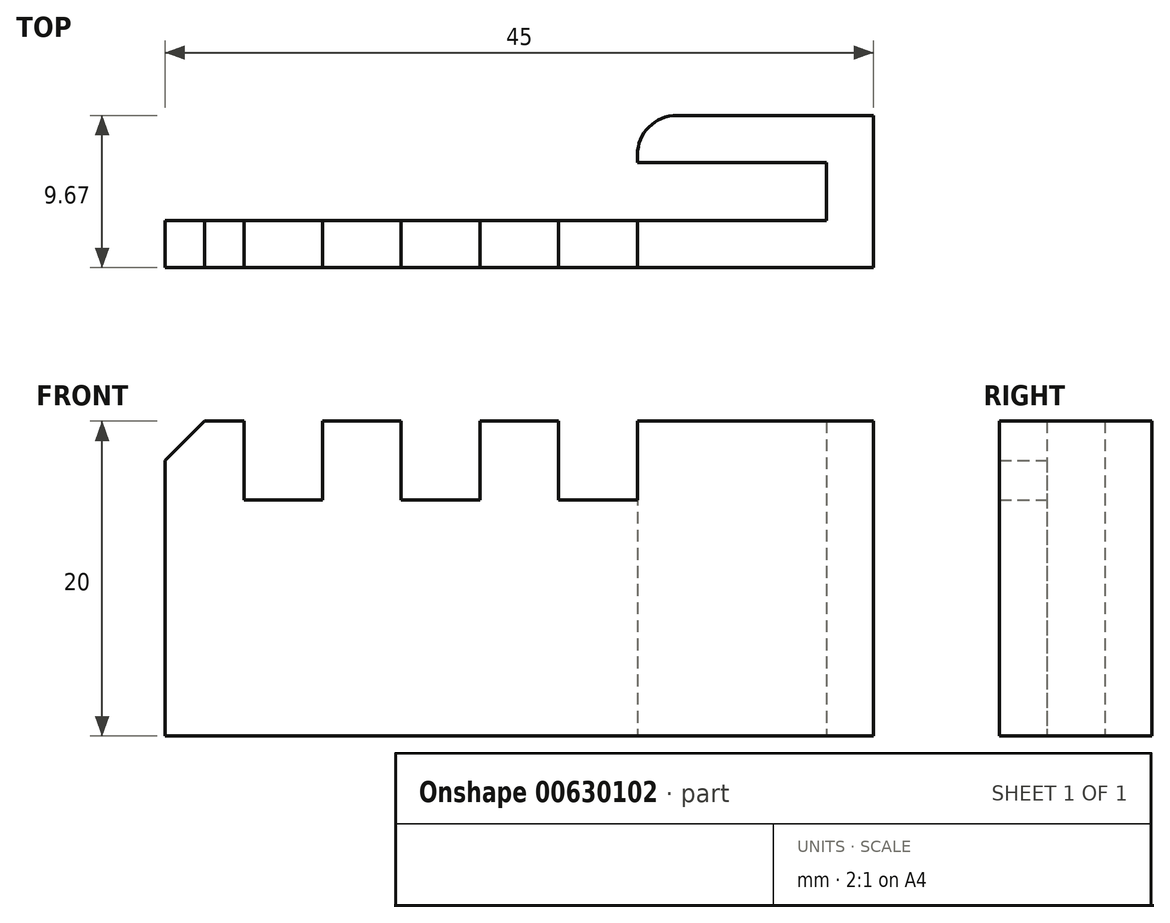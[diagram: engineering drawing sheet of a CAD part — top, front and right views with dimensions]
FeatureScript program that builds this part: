
annotation { "Feature Type Name" : "Feature", "Feature Type Description" : "" }
export const myFeature = defineFeature(function(context is Context, id is Id, definition is map)
    precondition{}
    {
        {
            var Q0;
            Q0=qCreatedBy(makeId("Top.planeOp"),FACE);
            var sketch = newSketch(context, id + "F0", { "sketchPlane" : qUnion([Q0])});
            skLineSegment(sketch, "E0", {"start": v(0, -4.53) * mm, "end": v(-15, -4.53) * mm});
            skLineSegment(sketch, "E1", {"start": v(-15, -4.53) * mm, "end": v(-15, -7.53) * mm});
            skLineSegment(sketch, "E2", {"start": v(-15, -7.53) * mm, "end": v(-3, -7.53) * mm});
            skLineSegment(sketch, "E3", {"start": v(-3, -7.53) * mm, "end": v(-3, -11.2) * mm});
            skLineSegment(sketch, "E4", {"start": v(-3, -11.2) * mm, "end": v(-45, -11.2) * mm});
            skLineSegment(sketch, "E5", {"start": v(0, -14.2) * mm, "end": v(-45, -14.2) * mm});
            skLineSegment(sketch, "E6", {"start": v(-45, -14.2) * mm, "end": v(-45, -11.2) * mm});
            skLineSegment(sketch, "E7", {"start": v(0, -4.53) * mm, "end": v(0, -14.2) * mm});
            skSolve(sketch);
        }
        {
            var Q0;
            Q0=makeQuery(id+"F0.imprint","IMPRINT",FACE,{"disambiguationData":[TD([[makeQuery(id+"F0.imprint","IMPRINT",EDGE,{"derivedFrom":sQuery(id+"F0.wireOp",EDGE,"E0")}),1.0]])]});
            extrude(context, id + "F1", {"entities" : qUnion([Q0]), "depth" : 20 * mm, "offsetDistance" : 25 * mm});
        }
        {
            var Q0;
            Q0=qCreatedBy(makeId("Front.planeOp"),FACE);
            var sketch = newSketch(context, id + "F2", { "sketchPlane" : qUnion([Q0])});
            skLineSegment(sketch, "E8.0.0", {"start": v(-45, 0) * mm, "end": v(0, 0) * mm});
            skLineSegment(sketch, "E8.0.1", {"start": v(0, 0) * mm, "end": v(0, 20) * mm});
            skLineSegment(sketch, "E8.0.2", {"start": v(0, 20) * mm, "end": v(-45, 20) * mm});
            skLineSegment(sketch, "E8.0.3", {"start": v(-45, 20) * mm, "end": v(-45, 0) * mm});
            skLineSegment(sketch, "E9", {"start": v(-15, 17.45) * mm, "end": v(-15, 20) * mm});
            skLineSegment(sketch, "E10", {"start": v(-15, 20) * mm, "end": v(-15, 15) * mm});
            skLineSegment(sketch, "E11", {"start": v(-15, 15) * mm, "end": v(-20, 15) * mm});
            skLineSegment(sketch, "E12", {"start": v(-20, 15) * mm, "end": v(-20, 20) * mm});
            skLineSegment(sketch, "E13", {"start": v(-20, 20) * mm, "end": v(-25, 20) * mm});
            skLineSegment(sketch, "E14", {"start": v(-25, 20) * mm, "end": v(-25, 15) * mm});
            skLineSegment(sketch, "E15", {"start": v(-25, 15) * mm, "end": v(-30, 15) * mm});
            skLineSegment(sketch, "E16", {"start": v(-30, 15) * mm, "end": v(-30, 20) * mm});
            skLineSegment(sketch, "E17", {"start": v(-30, 20) * mm, "end": v(-35, 20) * mm});
            skLineSegment(sketch, "E18", {"start": v(-35, 20) * mm, "end": v(-35, 15) * mm});
            skLineSegment(sketch, "E19", {"start": v(-15, 20) * mm, "end": v(0, 20) * mm});
            skLineSegment(sketch, "E20", {"start": v(-35, 15) * mm, "end": v(-40, 15) * mm});
            skLineSegment(sketch, "E21", {"start": v(-40, 15) * mm, "end": v(-40, 20) * mm});
            skSolve(sketch);
        }
        {
            var Q0;
            {var subQ0=sQuery(id+"F2.wireOp",EDGE,"p39oFGg6-OyMy-OwiJ-dlir-hBi66J1yGtTy");Q0=makeQuery(id+"F2.imprint","IMPRINT",FACE,{"disambiguationData":[TD([[makeQuery(id+"F2.imprint","IMPRINT",EDGE,{"derivedFrom":subQ0}),1.0]])]});}
            var Q1;
            {var subQ0=sQuery(id+"F2.wireOp",EDGE,"QODlYd0c-C4PW-zkeU-aZbA-vr5giQBnZzte");Q1=makeQuery(id+"F2.imprint","IMPRINT",FACE,{"disambiguationData":[TD([[makeQuery(id+"F2.imprint","IMPRINT",EDGE,{"derivedFrom":subQ0}),1.0]])]});}
            var Q2;
            {var subQ0=sQuery(id+"F2.wireOp",EDGE,"4xKgk40Y-SCAd-XMLl-Py7b-CMe8KArE31fU");Q2=makeQuery(id+"F2.imprint","IMPRINT",FACE,{"disambiguationData":[TD([[makeQuery(id+"F2.imprint","IMPRINT",EDGE,{"derivedFrom":subQ0}),1.0]])]});}
            var Q3;
            {var subQ0=sQuery(id+"F2.wireOp",EDGE,"CYAmrffy-ebrT-692H-EbRy-YjbJ9vrfb0BI");Q3=makeQuery(id+"F2.imprint","IMPRINT",FACE,{"disambiguationData":[TD([[makeQuery(id+"F2.imprint","IMPRINT",EDGE,{"derivedFrom":subQ0}),1.0]])]});}
            var Q4;
            {var subQ0=sQuery(id+"F2.wireOp",EDGE,"4ANwyr2W-lThm-HwLl-JWs1-NF0Ujadkufbg");Q4=makeQuery(id+"F2.imprint","IMPRINT",FACE,{"disambiguationData":[TD([[makeQuery(id+"F2.imprint","IMPRINT",EDGE,{"derivedFrom":subQ0}),1.0]])]});}
            var Q5;
            {var subQ0=sQuery(id+"F2.wireOp",EDGE,"E11");Q5=makeQuery(id+"F2.imprint","IMPRINT",FACE,{"disambiguationData":[TD([[makeQuery(id+"F2.imprint","IMPRINT",EDGE,{"derivedFrom":subQ0}),-1.0]])]});}
            var Q6;
            {var subQ0=sQuery(id+"F2.wireOp",EDGE,"E14");Q6=makeQuery(id+"F2.imprint","IMPRINT",FACE,{"disambiguationData":[TD([[makeQuery(id+"F2.imprint","IMPRINT",EDGE,{"derivedFrom":subQ0}),-1.0]])]});}
            var Q7;
            {var subQ0=sQuery(id+"F2.wireOp",EDGE,"E18");Q7=makeQuery(id+"F2.imprint","IMPRINT",FACE,{"disambiguationData":[TD([[makeQuery(id+"F2.imprint","IMPRINT",EDGE,{"derivedFrom":subQ0}),-1.0]])]});}
            extrude(context, id + "F3", {"entities" : qUnion([Q0, Q1, Q2, Q3, Q4, Q5, Q6, Q7]), "operationType" : NewBodyOperationType.REMOVE, "endBound" : BoundingType.THROUGH_ALL, "depth" : 25 * mm, "offsetDistance" : 25 * mm});
        }
        {
            var Q0;
            Q0=makeQuery(id+"F1.opExtrude","CAP_EDGE",EDGE,{"disambiguationData":[OSD([sQuery(id+"F0.wireOp",EDGE,"E6")])],"isStart":false});
            chamfer(context, id + "F4", {"entities" : qUnion([Q0]), "width" : 2.5 * mm, "tangentPropagation" : true});
        }
        {
            var Q0;
            Q0=makeQuery(id+"F1.opExtrude","SWEPT_EDGE",EDGE,{"disambiguationData":[OSD([sQuery(id+"F0.wireOp",EDGE,"E0"),sQuery(id+"F0.wireOp",EDGE,"E1")])]});
            fillet(context, id + "F5", {"entities" : qUnion([Q0]), "radius" : 2.5 * mm, "tangentPropagation" : true, "allowEdgeOverflow" : false});
        }
    });
